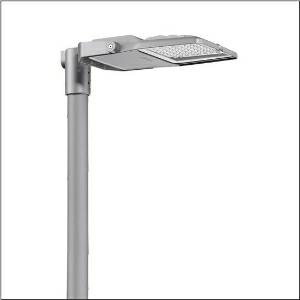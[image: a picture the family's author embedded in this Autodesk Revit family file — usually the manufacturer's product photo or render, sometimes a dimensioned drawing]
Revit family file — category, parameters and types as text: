
# Revit family: floodlight_fl_21_iq_mini___pl33t_5xa7772c4f3a_1e48
name_source: partatom
category: Lighting Fixtures
units: mm (PartAtom-declared; Revit-internal decimal feet)

## family parameters
Cut with Voids When Loaded = No
Host = Face
Light Source = No
Part Type = Normal
Room Calculation Point = No
Round Connector Dimension = Use Diameter
Shared = No

## types (1)
- --- (1 x LED, 12570 lm, 87.2 W, 4000K)
    Apparent Load = 87 VA
    CIE Flux Codes = 26 75 99 100 100
    Color Rendering = 70
    Color Temperature = 4000K
    Default Elevation = 1800 mm
    Description = Floodlight FL 21 iQ mini, floodlight, primary light control with lens, of PMMA, primary optical cover: protective disc, of toughened safety glass, transparent, light distribution: PL33T, light emission: direct distribution, installation type: surface-mounted, LED, High Power LED, rated luminous flux: 12.570lm, luminous efficacy: 144lm/W, light colour: 740, colour temperature: 4000K, control gear: iQ Street-Remote/DALI, control: Auto-Match, Temp-Guard, Night-Set, Smart-Wire, Desk-Remote (wireless, voltage-free reading and setting of iQ features in the workshop via application-optimized NFC function/RFID function), optimised constant luminous flux control (CLO 2.0), Light-Fading, Lumen-Switch, with terminal, 6-pole, mains connection: 220..240V, AC, 50/60Hz, start of lifetime: 87W, end of service life: 92W, reduction: 40W, luminaire housing, of diecast aluminium, powder-coated, Siteco® metallic grey (DB 702S), corrosivity category C5 mid according to DIN EN ISO 12944, suitable for swimming pools, chlorine-resistant, sealing non-destructively replaceable, please order mast flange separately, mast bracket, of steel, galvanised, powder-coated, protection rating (complete): IP66, insulation class (complete): insulation class II (safety insulation), certification: CE, ENEC, VDE, protection symbol: D, impact resistance: IK08, permissible operating ambient temperature: -40..+40°C, permissible operating ambient temperature for outdoor applications: -40..+50°C, standard: DIN EN 12944, LABS conformity tested according to VDMA 24364:2018-05, packaging unit: 1 piece

Light Distribution: PL33T
    Height = 70 mm
    Lamp = 1 x LED
    Lamp Light Flux = 12570 lm
    Lamp Power = 87.2 W
    Lamp count = 1
    Length = 485 mm
    Luminous efficacy = 144 lm/W
    Manufacturer = Siteco
    ModVariant = No
    Model = 5XA7772C4F3A
    Number of Poles = 1
    OnlyDefault = Yes
    Power Factor = 1
    Product Name = Floodlight FL 21 iQ mini | PL33T
    Product group = floodlight | pylon annexe
    ProductGroupID = 6201
    Protection Class = Protection class II
    Protection Degree = IP 66
    RLX_Detail_Level = 1
    RLX_Emergency_Light_Flux = 0 lm
    RLX_Emergency_Type = 0
    RLX_Emergency_Type_DB = No
    RlxData = <blob elided: 101337 chars, md5=d505d0f2>
    Socket = socket
    Standby Power = 0 W
    System Light Flux = 12570 lm
    System Power = 87 W
    Type Comments = factory setting: luminous flux: 100 % | dim-lin: 254 | 456 mA
    Type Image = l_1007125.jpg
    URL = http://relux.com
    VarID = @adj_170789
    Voltage = 0 V
    Weight = 0.00 kg
    Width = 337 mm

## geometry (parser evidence)
native form markers: Blend x4, Sweep x14
no freeform markers — native parametric forms only
